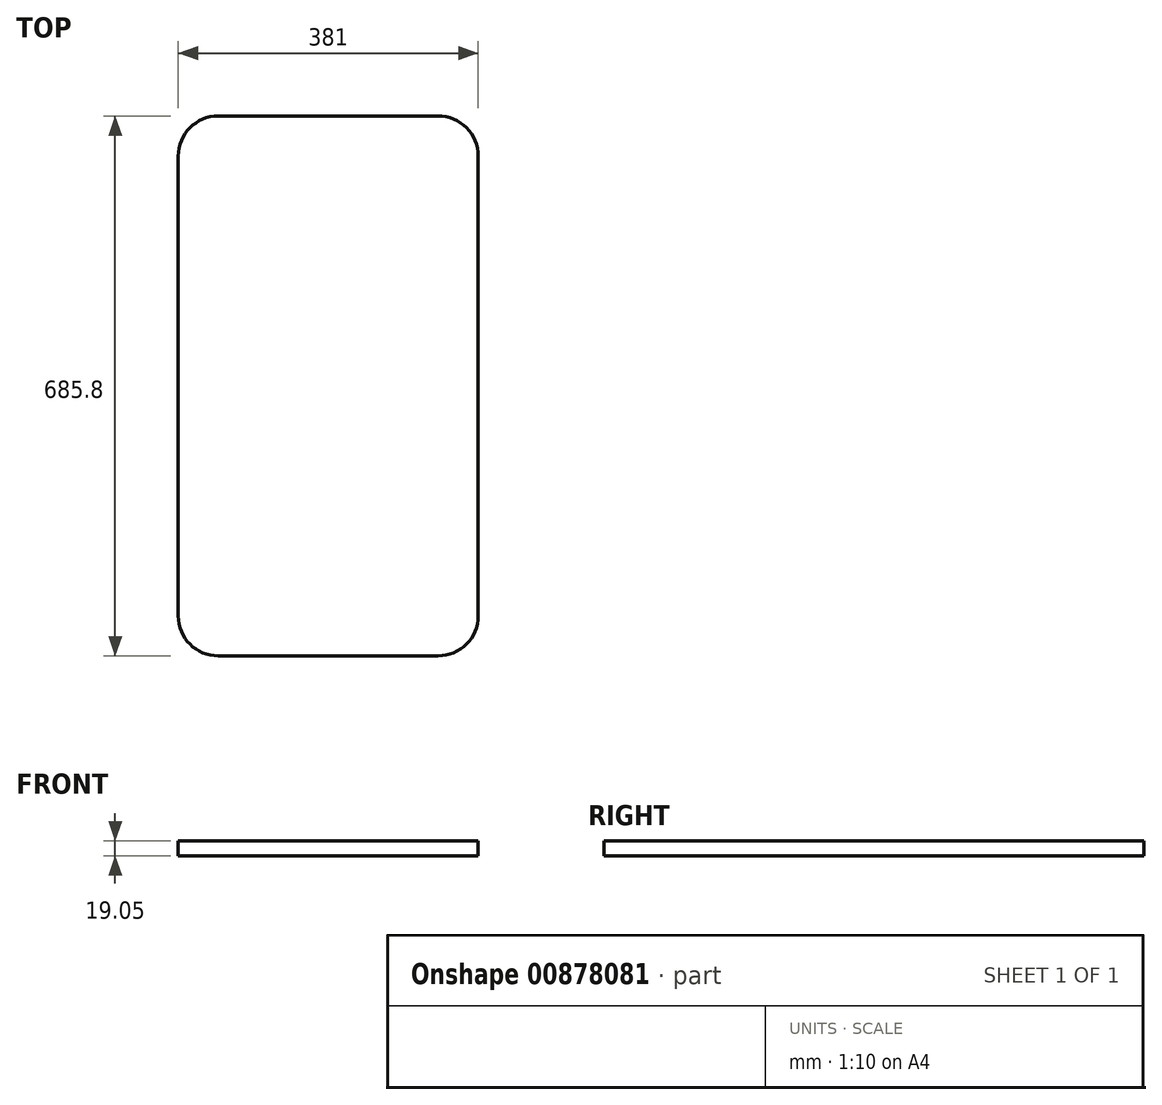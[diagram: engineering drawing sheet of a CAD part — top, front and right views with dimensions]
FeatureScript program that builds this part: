
annotation { "Feature Type Name" : "Feature", "Feature Type Description" : "" }
export const myFeature = defineFeature(function(context is Context, id is Id, definition is map)
    precondition{}
    {
        {
            var Q0;
            Q0=qCreatedBy(makeId("Top.planeOp"),FACE);
            var sketch = newSketch(context, id + "F0", { "sketchPlane" : qUnion([Q0])});
            skLineSegment(sketch, "E0.bottom", {"start": v(0, 0) * mm, "end": v(381, 0) * mm});
            skLineSegment(sketch, "E0.top", {"start": v(0, 685.8) * mm, "end": v(381, 685.8) * mm});
            skLineSegment(sketch, "E0.left", {"start": v(0, 0) * mm, "end": v(0, 685.8) * mm});
            skLineSegment(sketch, "E0.right", {"start": v(381, 0) * mm, "end": v(381, 685.8) * mm});
            skSolve(sketch);
        }
        {
            var Q0;
            Q0=qSketchRegion(id+"F0",true);
            extrude(context, id + "F1", {"entities" : qUnion([Q0]), "depth" : 19.05 * mm, "offsetDistance" : 25.4 * mm});
        }
        {
            var Q0;
            Q0=makeQuery(id+"F1.opExtrude","SWEPT_EDGE",EDGE,{"disambiguationData":[OSD([sQuery(id+"F0.wireOp",EDGE,"E0.bottom"),sQuery(id+"F0.wireOp",EDGE,"E0.right")])]});
            var Q1;
            Q1=makeQuery(id+"F1.opExtrude","SWEPT_EDGE",EDGE,{"disambiguationData":[OSD([sQuery(id+"F0.wireOp",EDGE,"E0.bottom"),sQuery(id+"F0.wireOp",EDGE,"E0.left")])]});
            var Q2;
            Q2=makeQuery(id+"F1.opExtrude","SWEPT_EDGE",EDGE,{"disambiguationData":[OSD([sQuery(id+"F0.wireOp",EDGE,"E0.top"),sQuery(id+"F0.wireOp",EDGE,"E0.right")])]});
            var Q3;
            Q3=makeQuery(id+"F1.opExtrude","SWEPT_EDGE",EDGE,{"disambiguationData":[OSD([sQuery(id+"F0.wireOp",EDGE,"E0.top"),sQuery(id+"F0.wireOp",EDGE,"E0.left")])]});
            fillet(context, id + "F2", {"entities" : qUnion([Q0, Q1, Q2, Q3]), "radius" : 50.8 * mm, "tangentPropagation" : true, "allowEdgeOverflow" : false});
        }
    });
